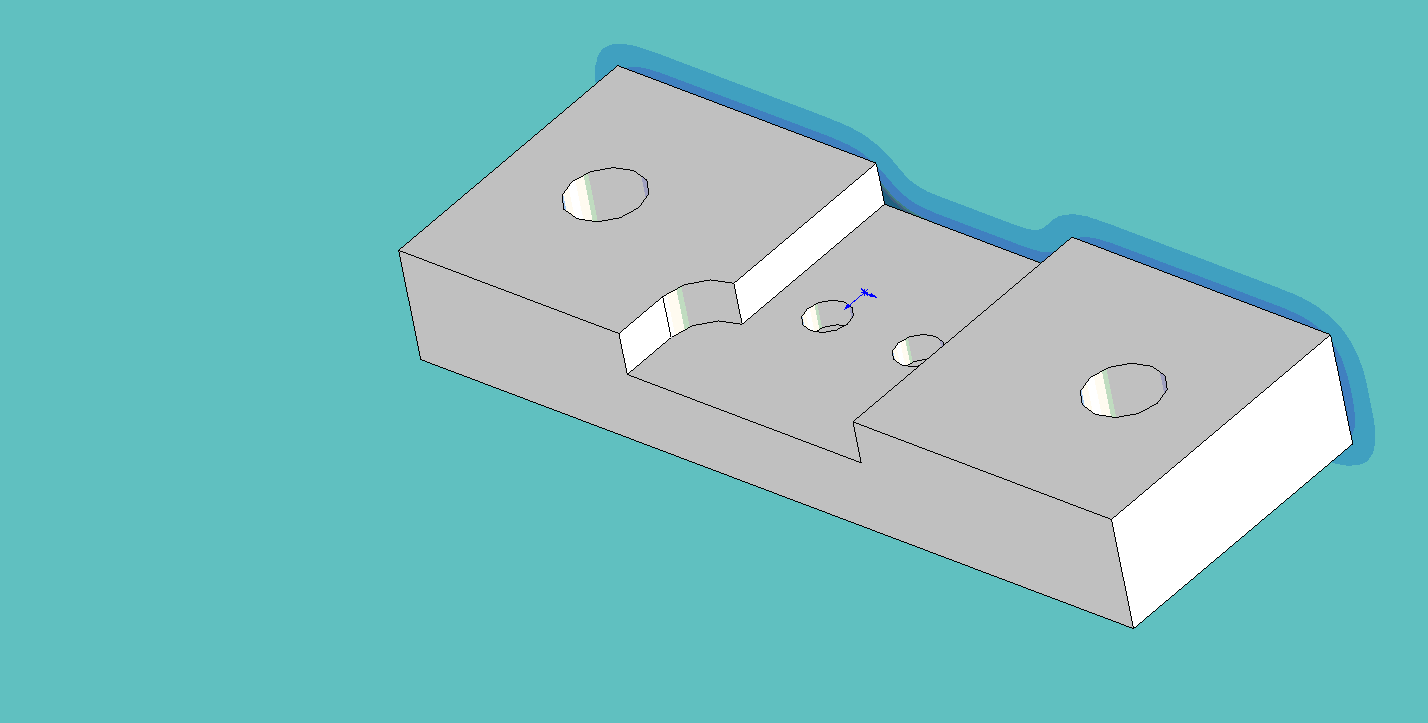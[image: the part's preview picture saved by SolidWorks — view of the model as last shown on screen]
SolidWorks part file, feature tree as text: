
SOLIDWORKS PART (.sldprt)
format: sldprt  version: not decoded by parser v0  size: 190,976 bytes
history: native  units: mm
features: sketch x4, plane x3, cut_extrude x3, material x1, extrude x1 (+10 scaffold rows collapsed)
feature tree (22):
  scaffold x10  (default folders/planes/origin — collapsed)
  material  "Matériau <non spécifié>"
  plane  "Plan de face"
  plane  "Plan de dessus"
  plane  "Plan de droite"
  sketch  "Esquisse1"  dims[c1.D3=5.2mm c1.D4=5.2mm c1.D6=3.1mm c1.D7=3.1mm c1.D8=3.1mm c1.D1=55.0mm c1.D2=20.0mm c2.D4=40.0mm c2.D5=20.0mm c2.D7=7.0mm c2.D8=3.5mm]
  extrude  "Extrusion1"  Depth=8mm
  sketch  "Esquisse2"  dims[D1=7.0mm]
  cut_extrude  "Enlèv. mat.-Extru.1"  Depth=1.5mm
  sketch  "Esquisse3"  dims[D1=6.0mm]
  cut_extrude  "Enlèv. mat.-Extru.2"  Depth=3.2mm
  sketch  "Esquisse4"  dims[D4=3.0mm D1=7.55mm D2=7.55mm D3=7.5mm D5=4.0mm]
  cut_extrude  "Enlèv. mat.-Extru.3"  Depth=3mm
decode coverage: 8 of 8 modeling features carry decoded parameters
note: suppression state not decoded; provenance and decode notes live in map.json
